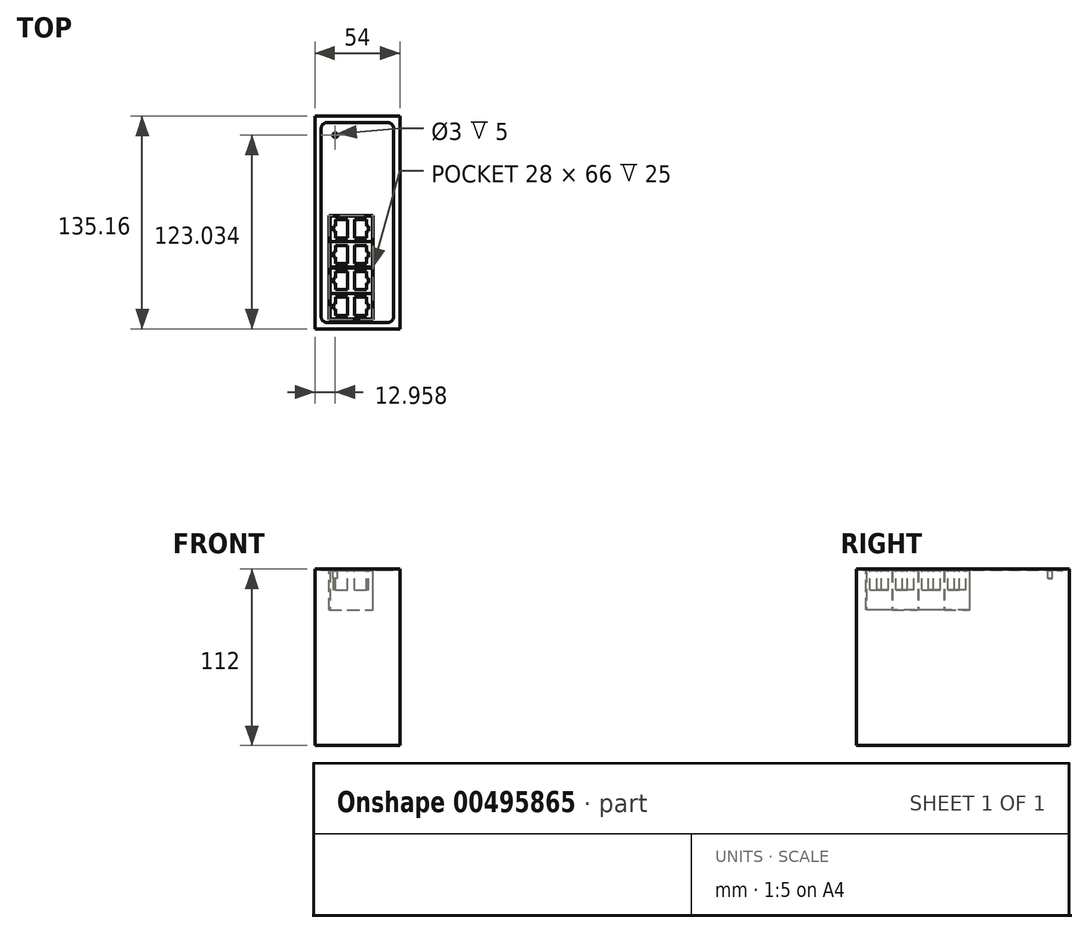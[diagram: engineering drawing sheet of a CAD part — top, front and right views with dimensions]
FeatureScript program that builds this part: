
annotation { "Feature Type Name" : "Feature", "Feature Type Description" : "" }
export const myFeature = defineFeature(function(context is Context, id is Id, definition is map)
    precondition{}
    {
        {
            var Q0;
            Q0=qCreatedBy(makeId("Right.planeOp"),FACE);
            var sketch = newSketch(context, id + "F0", { "sketchPlane" : qUnion([Q0])});
            skLineSegment(sketch, "E0.bottom", {"start": v(-67.57, 0) * mm, "end": v(67.57, 0) * mm});
            skLineSegment(sketch, "E0.top", {"start": v(-67.58, 112) * mm, "end": v(67.58, 112) * mm});
            skLineSegment(sketch, "E0.left", {"start": v(-67.58, 0) * mm, "end": v(-67.58, 112) * mm});
            skLineSegment(sketch, "E0.right", {"start": v(67.58, 0) * mm, "end": v(67.58, 112) * mm});
            skSolve(sketch);
        }
        {
            var Q0;
            Q0=qSketchRegion(id+"F0",true);
            extrude(context, id + "F1", {"entities" : qUnion([Q0]), "endBound" : BoundingType.SYMMETRIC, "depth" : 54 * mm});
        }
        {
            var Q0;
            Q0=makeQuery(id+"F1.opExtrude","SWEPT_FACE",FACE,{"disambiguationData":[OSD([sQuery(id+"F0.wireOp",EDGE,"E0.top")])]});
            var sketch = newSketch(context, id + "F2", { "sketchPlane" : qUnion([Q0])});
            skLineSegment(sketch, "E1.bottom", {"start": v(19, 63.58) * mm, "end": v(-19, 63.58) * mm});
            skLineSegment(sketch, "E1.top", {"start": v(19, -63.58) * mm, "end": v(-19, -63.58) * mm});
            skLineSegment(sketch, "E1.left", {"start": v(23, 59.58) * mm, "end": v(23, -59.58) * mm});
            skLineSegment(sketch, "E1.right", {"start": v(-23, 59.58) * mm, "end": v(-23, -59.58) * mm});
            skPoint(sketch, "E1.middle", {"position": v(0, 0) * mm});
            skPoint(sketch, "E2.visualSharp", {"position": v(-23, 63.58) * mm});
            skArc(sketch, "E2.filletArc", {"start": v(-19, 63.58) * mm, "mid": v(-21.83, 62.4) * mm, "end": v(-23, 59.58) * mm});
            skPoint(sketch, "E3.visualSharp", {"position": v(23, 63.58) * mm});
            skArc(sketch, "E3.filletArc", {"start": v(23, 59.58) * mm, "mid": v(21.83, 62.4) * mm, "end": v(19, 63.58) * mm});
            skPoint(sketch, "E4.visualSharp", {"position": v(23, -63.58) * mm});
            skArc(sketch, "E4.filletArc", {"start": v(19, -63.58) * mm, "mid": v(21.83, -62.4) * mm, "end": v(23, -59.58) * mm});
            skPoint(sketch, "E5.visualSharp", {"position": v(-23, -63.58) * mm});
            skArc(sketch, "E5.filletArc", {"start": v(-23, -59.58) * mm, "mid": v(-21.83, -62.4) * mm, "end": v(-19, -63.58) * mm});
            skSolve(sketch);
        }
        {
            var Q0;
            Q0=qSketchRegion(id+"F2",true);
            extrude(context, id + "F3", {"entities" : qUnion([Q0]), "operationType" : NewBodyOperationType.REMOVE, "oppositeDirection" : true, "depth" : 1 * mm});
        }
        {
            var Q0;
            Q0=makeQuery(id+"F3.boolean.opBoolean","COPY",FACE,{"derivedFrom":makeQuery(id+"F3.opExtrude","CAP_FACE",FACE,{"disambiguationData":[OSD([sQuery(id+"F2.wireOp",EDGE,"E1.bottom"),sQuery(id+"F2.wireOp",EDGE,"E1.top"),sQuery(id+"F2.wireOp",EDGE,"E1.left"),sQuery(id+"F2.wireOp",EDGE,"E1.right"),sQuery(id+"F2.wireOp",EDGE,"E2.filletArc"),sQuery(id+"F2.wireOp",EDGE,"E3.filletArc"),sQuery(id+"F2.wireOp",EDGE,"E4.filletArc"),sQuery(id+"F2.wireOp",EDGE,"E5.filletArc")])],"isStart":false})});
            var sketch = newSketch(context, id + "F4", { "sketchPlane" : qUnion([Q0])});
            skLineSegment(sketch, "E6.bottom", {"start": v(-18, 4.42) * mm, "end": v(10, 4.43) * mm});
            skLineSegment(sketch, "E6.top", {"start": v(-18, -61.58) * mm, "end": v(10, -61.58) * mm});
            skLineSegment(sketch, "E6.left", {"start": v(-18, 4.43) * mm, "end": v(-18, -61.58) * mm});
            skLineSegment(sketch, "E6.right", {"start": v(10, 4.43) * mm, "end": v(10, -61.58) * mm});
            skSolve(sketch);
        }
        {
            var Q0;
            Q0=qSketchRegion(id+"F4",true);
            extrude(context, id + "F5", {"entities" : qUnion([Q0]), "operationType" : NewBodyOperationType.REMOVE, "oppositeDirection" : true, "depth" : 25 * mm});
        }
        {
            var Q0;
            Q0=makeQuery(id+"F5.boolean.opBoolean","COPY",FACE,{"derivedFrom":makeQuery(id+"F5.opExtrude","CAP_FACE",FACE,{"disambiguationData":[OSD([sQuery(id+"F4.wireOp",EDGE,"E6.bottom"),sQuery(id+"F4.wireOp",EDGE,"E6.top"),sQuery(id+"F4.wireOp",EDGE,"E6.left"),sQuery(id+"F4.wireOp",EDGE,"E6.right")])],"isStart":false})});
            var sketch = newSketch(context, id + "F6", { "sketchPlane" : qUnion([Q0])});
            skLineSegment(sketch, "E7", {"start": v(-18, -28.58) * mm, "end": v(10, -28.58) * mm, "construction": true});
            skLineSegment(sketch, "E8", {"start": v(-4, 4.42) * mm, "end": v(-4, -61.58) * mm, "construction": true});
            skLineSegment(sketch, "E9.bottom", {"start": v(-17.5, -12.2) * mm, "end": v(9.5, -12.2) * mm});
            skLineSegment(sketch, "E9.top", {"start": v(-17.5, -28.4) * mm, "end": v(9.5, -28.4) * mm});
            skLineSegment(sketch, "E9.left", {"start": v(-17.5, -12.2) * mm, "end": v(-17.5, -28.4) * mm});
            skLineSegment(sketch, "E9.right", {"start": v(9.5, -12.2) * mm, "end": v(9.5, -28.4) * mm});
            skLineSegment(sketch, "E10", {"start": v(-18, -28.57) * mm, "end": v(10, 4.42) * mm, "construction": true});
            skLineSegment(sketch, "E11", {"start": v(-4, -12.08) * mm, "end": v(-18, -12.08) * mm, "construction": true});
            skLineSegment(sketch, "E12.MirrorCS", {"start": v(9.5, -11.95) * mm, "end": v(9.5, 4.25) * mm});
            skLineSegment(sketch, "E13.MirrorCS", {"start": v(-17.5, 4.25) * mm, "end": v(9.5, 4.25) * mm});
            skLineSegment(sketch, "E14.MirrorCS", {"start": v(-17.5, -11.95) * mm, "end": v(9.5, -11.95) * mm});
            skLineSegment(sketch, "E15.MirrorCS", {"start": v(-17.5, -11.95) * mm, "end": v(-17.5, 4.25) * mm});
            skLineSegment(sketch, "E16.MirrorCS", {"start": v(9.5, -44.95) * mm, "end": v(9.5, -28.75) * mm});
            skLineSegment(sketch, "E17.MirrorCS", {"start": v(-17.5, -28.75) * mm, "end": v(9.5, -28.75) * mm});
            skLineSegment(sketch, "E18.MirrorCS", {"start": v(-17.5, -44.95) * mm, "end": v(-17.5, -28.75) * mm});
            skLineSegment(sketch, "E19.MirrorCS", {"start": v(-17.5, -44.95) * mm, "end": v(9.5, -44.95) * mm});
            skLineSegment(sketch, "E20.MirrorCS", {"start": v(9.5, -45.2) * mm, "end": v(9.5, -61.4) * mm});
            skLineSegment(sketch, "E21.MirrorCS", {"start": v(-17.5, -45.2) * mm, "end": v(9.5, -45.2) * mm});
            skLineSegment(sketch, "E22.MirrorCS", {"start": v(-17.5, -61.4) * mm, "end": v(9.5, -61.4) * mm});
            skLineSegment(sketch, "E23.MirrorCS", {"start": v(-17.5, -45.2) * mm, "end": v(-17.5, -61.4) * mm});
            skSolve(sketch);
        }
        {
            var Q0;
            Q0=qSketchRegion(id+"F6",true);
            extrude(context, id + "F7", {"entities" : qUnion([Q0]), "depth" : 25 * mm});
        }
        {
            var Q0;
            Q0=makeQuery(id+"F7.opExtrude","CAP_FACE",FACE,{"disambiguationData":[OSD([sQuery(id+"F6.wireOp",EDGE,"E12.MirrorCS"),sQuery(id+"F6.wireOp",EDGE,"E13.MirrorCS"),sQuery(id+"F6.wireOp",EDGE,"E14.MirrorCS"),sQuery(id+"F6.wireOp",EDGE,"E15.MirrorCS")])],"isStart":false});
            var sketch = newSketch(context, id + "F8", { "sketchPlane" : qUnion([Q0])});
            skLineSegment(sketch, "E24", {"start": v(-17.5, -3.85) * mm, "end": v(9.5, -3.85) * mm, "construction": true});
            skLineSegment(sketch, "E25", {"start": v(-4, 4.25) * mm, "end": v(-4, -69.59) * mm, "construction": true});
            skLineSegment(sketch, "E26", {"start": v(-6.25, -9.69) * mm, "end": v(-6.25, 2) * mm});
            skLineSegment(sketch, "E27", {"start": v(-6.25, 2) * mm, "end": v(-13.72, 2) * mm});
            skLineSegment(sketch, "E28", {"start": v(-13.72, 2) * mm, "end": v(-13.72, -2.35) * mm});
            skLineSegment(sketch, "E29", {"start": v(-13.72, -2.35) * mm, "end": v(-15.22, -2.35) * mm});
            skLineSegment(sketch, "E30", {"start": v(-15.22, -2.35) * mm, "end": v(-15.22, -5.35) * mm});
            skLineSegment(sketch, "E31", {"start": v(-15.22, -5.35) * mm, "end": v(-13.72, -5.35) * mm});
            skLineSegment(sketch, "E32", {"start": v(-13.72, -5.35) * mm, "end": v(-13.72, -9.69) * mm});
            skLineSegment(sketch, "E33", {"start": v(-13.72, -9.69) * mm, "end": v(-6.25, -9.69) * mm});
            skLineSegment(sketch, "E34.MirrorCS", {"start": v(5.72, -2.35) * mm, "end": v(7.22, -2.35) * mm});
            skLineSegment(sketch, "E35.MirrorCS", {"start": v(7.22, -2.35) * mm, "end": v(7.22, -5.35) * mm});
            skLineSegment(sketch, "E36.MirrorCS", {"start": v(7.22, -5.35) * mm, "end": v(5.72, -5.35) * mm});
            skLineSegment(sketch, "E37.MirrorCS", {"start": v(5.72, -5.35) * mm, "end": v(5.72, -9.69) * mm});
            skLineSegment(sketch, "E38.MirrorCS", {"start": v(5.72, -9.69) * mm, "end": v(-1.75, -9.69) * mm});
            skLineSegment(sketch, "E39.MirrorCS", {"start": v(-1.75, -9.69) * mm, "end": v(-1.75, 2) * mm});
            skLineSegment(sketch, "E40.MirrorCS", {"start": v(5.72, 2) * mm, "end": v(5.72, -2.35) * mm});
            skLineSegment(sketch, "E41.MirrorCS", {"start": v(-1.75, 2) * mm, "end": v(5.72, 2) * mm});
            skPoint(sketch, "E42.0", {"position": v(-18, -28.58) * mm});
            skLineSegment(sketch, "E43", {"start": v(-18, -28.58) * mm, "end": v(13.25, -28.58) * mm, "construction": true});
            skPoint(sketch, "E44.0", {"position": v(10, 4.43) * mm});
            skLineSegment(sketch, "E45", {"start": v(-18, -28.57) * mm, "end": v(10, 4.42) * mm, "construction": true});
            skLineSegment(sketch, "E46", {"start": v(-4, -12.08) * mm, "end": v(-18.06, -12.08) * mm, "construction": true});
            skLineSegment(sketch, "E47.MirrorCS", {"start": v(5.72, -14.46) * mm, "end": v(-1.75, -14.46) * mm});
            skLineSegment(sketch, "E48.MirrorCS", {"start": v(5.72, -18.8) * mm, "end": v(5.72, -14.46) * mm});
            skLineSegment(sketch, "E49.MirrorCS", {"start": v(7.22, -18.8) * mm, "end": v(5.72, -18.8) * mm});
            skLineSegment(sketch, "E50.MirrorCS", {"start": v(7.22, -21.8) * mm, "end": v(7.22, -18.8) * mm});
            skLineSegment(sketch, "E51.MirrorCS", {"start": v(5.72, -21.8) * mm, "end": v(7.22, -21.8) * mm});
            skLineSegment(sketch, "E52.MirrorCS", {"start": v(5.72, -26.14) * mm, "end": v(5.72, -21.8) * mm});
            skLineSegment(sketch, "E53.MirrorCS", {"start": v(-1.75, -26.14) * mm, "end": v(5.72, -26.14) * mm});
            skLineSegment(sketch, "E54.MirrorCS", {"start": v(-1.75, -14.46) * mm, "end": v(-1.75, -26.14) * mm});
            skLineSegment(sketch, "E55.MirrorCS", {"start": v(-6.25, -14.46) * mm, "end": v(-6.25, -26.14) * mm});
            skLineSegment(sketch, "E56.MirrorCS", {"start": v(-13.72, -14.46) * mm, "end": v(-6.25, -14.46) * mm});
            skLineSegment(sketch, "E57.MirrorCS", {"start": v(-13.72, -18.8) * mm, "end": v(-13.72, -14.46) * mm});
            skLineSegment(sketch, "E58.MirrorCS", {"start": v(-15.22, -18.8) * mm, "end": v(-13.72, -18.8) * mm});
            skLineSegment(sketch, "E59.MirrorCS", {"start": v(-15.22, -21.8) * mm, "end": v(-15.22, -18.8) * mm});
            skLineSegment(sketch, "E60.MirrorCS", {"start": v(-13.72, -21.8) * mm, "end": v(-15.22, -21.8) * mm});
            skLineSegment(sketch, "E61.MirrorCS", {"start": v(-6.25, -26.14) * mm, "end": v(-13.72, -26.14) * mm});
            skLineSegment(sketch, "E62.MirrorCS", {"start": v(-13.72, -26.14) * mm, "end": v(-13.72, -21.8) * mm});
            skLineSegment(sketch, "E63.MirrorCS", {"start": v(-1.75, -31) * mm, "end": v(5.72, -31) * mm});
            skLineSegment(sketch, "E64.MirrorCS", {"start": v(5.72, -31) * mm, "end": v(5.72, -35.35) * mm});
            skLineSegment(sketch, "E65.MirrorCS", {"start": v(5.72, -35.35) * mm, "end": v(7.22, -35.35) * mm});
            skLineSegment(sketch, "E66.MirrorCS", {"start": v(7.22, -35.35) * mm, "end": v(7.22, -38.35) * mm});
            skLineSegment(sketch, "E67.MirrorCS", {"start": v(7.22, -38.35) * mm, "end": v(5.72, -38.35) * mm});
            skLineSegment(sketch, "E68.MirrorCS", {"start": v(5.72, -38.35) * mm, "end": v(5.72, -42.69) * mm});
            skLineSegment(sketch, "E69.MirrorCS", {"start": v(5.72, -42.69) * mm, "end": v(-1.75, -42.69) * mm});
            skLineSegment(sketch, "E70.MirrorCS", {"start": v(-1.75, -42.69) * mm, "end": v(-1.75, -31) * mm});
            skLineSegment(sketch, "E71.MirrorCS", {"start": v(-6.25, -42.69) * mm, "end": v(-6.25, -31) * mm});
            skLineSegment(sketch, "E72.MirrorCS", {"start": v(-6.25, -31) * mm, "end": v(-13.72, -31) * mm});
            skLineSegment(sketch, "E73.MirrorCS", {"start": v(-13.72, -31) * mm, "end": v(-13.72, -35.35) * mm});
            skLineSegment(sketch, "E74.MirrorCS", {"start": v(-13.72, -35.35) * mm, "end": v(-15.22, -35.35) * mm});
            skLineSegment(sketch, "E75.MirrorCS", {"start": v(-15.22, -35.35) * mm, "end": v(-15.22, -38.35) * mm});
            skLineSegment(sketch, "E76.MirrorCS", {"start": v(-15.22, -38.35) * mm, "end": v(-13.72, -38.35) * mm});
            skLineSegment(sketch, "E77.MirrorCS", {"start": v(-13.72, -38.35) * mm, "end": v(-13.72, -42.69) * mm});
            skLineSegment(sketch, "E78.MirrorCS", {"start": v(-13.72, -42.69) * mm, "end": v(-6.25, -42.69) * mm});
            skLineSegment(sketch, "E79.MirrorCS", {"start": v(5.72, -47.46) * mm, "end": v(-1.75, -47.46) * mm});
            skLineSegment(sketch, "E80.MirrorCS", {"start": v(5.72, -51.8) * mm, "end": v(5.72, -47.46) * mm});
            skLineSegment(sketch, "E81.MirrorCS", {"start": v(7.22, -51.8) * mm, "end": v(5.72, -51.8) * mm});
            skLineSegment(sketch, "E82.MirrorCS", {"start": v(7.22, -54.8) * mm, "end": v(7.22, -51.8) * mm});
            skLineSegment(sketch, "E83.MirrorCS", {"start": v(5.72, -54.8) * mm, "end": v(7.22, -54.8) * mm});
            skLineSegment(sketch, "E84.MirrorCS", {"start": v(5.72, -59.14) * mm, "end": v(5.72, -54.8) * mm});
            skLineSegment(sketch, "E85.MirrorCS", {"start": v(-1.75, -59.14) * mm, "end": v(5.72, -59.14) * mm});
            skLineSegment(sketch, "E86.MirrorCS", {"start": v(-1.75, -47.46) * mm, "end": v(-1.75, -59.14) * mm});
            skLineSegment(sketch, "E87.MirrorCS", {"start": v(-6.25, -47.46) * mm, "end": v(-6.25, -59.14) * mm});
            skLineSegment(sketch, "E88.MirrorCS", {"start": v(-13.72, -47.46) * mm, "end": v(-6.25, -47.46) * mm});
            skLineSegment(sketch, "E89.MirrorCS", {"start": v(-13.72, -51.8) * mm, "end": v(-13.72, -47.46) * mm});
            skLineSegment(sketch, "E90.MirrorCS", {"start": v(-15.22, -51.8) * mm, "end": v(-13.72, -51.8) * mm});
            skLineSegment(sketch, "E91.MirrorCS", {"start": v(-15.22, -54.8) * mm, "end": v(-15.22, -51.8) * mm});
            skLineSegment(sketch, "E92.MirrorCS", {"start": v(-13.72, -54.8) * mm, "end": v(-15.22, -54.8) * mm});
            skLineSegment(sketch, "E93.MirrorCS", {"start": v(-6.25, -59.14) * mm, "end": v(-13.72, -59.14) * mm});
            skLineSegment(sketch, "E94.MirrorCS", {"start": v(-13.72, -59.14) * mm, "end": v(-13.72, -54.8) * mm});
            skSolve(sketch);
        }
        {
            var Q0;
            Q0=qSketchRegion(id+"F8",true);
            extrude(context, id + "F9", {"entities" : qUnion([Q0]), "operationType" : NewBodyOperationType.REMOVE, "oppositeDirection" : true, "depth" : 12.32 * mm});
        }
        {
            var Q0;
            Q0=makeQuery(id+"F3.boolean.opBoolean","COPY",FACE,{"derivedFrom":makeQuery(id+"F3.opExtrude","CAP_FACE",FACE,{"disambiguationData":[OSD([sQuery(id+"F2.wireOp",EDGE,"E1.bottom"),sQuery(id+"F2.wireOp",EDGE,"E1.top"),sQuery(id+"F2.wireOp",EDGE,"E1.left"),sQuery(id+"F2.wireOp",EDGE,"E1.right"),sQuery(id+"F2.wireOp",EDGE,"E2.filletArc"),sQuery(id+"F2.wireOp",EDGE,"E3.filletArc"),sQuery(id+"F2.wireOp",EDGE,"E4.filletArc"),sQuery(id+"F2.wireOp",EDGE,"E5.filletArc")])],"isStart":false})});
            var sketch = newSketch(context, id + "F10", { "sketchPlane" : qUnion([Q0])});
            skCircle(sketch, "E95", {"center": v(-14.04, 55.45) * mm, "radius": 1.5 * mm});
            skSolve(sketch);
        }
        {
            var Q0;
            Q0=qSketchRegion(id+"F10",true);
            extrude(context, id + "F11", {"entities" : qUnion([Q0]), "operationType" : NewBodyOperationType.REMOVE, "oppositeDirection" : true, "depth" : 5 * mm});
        }
    });
